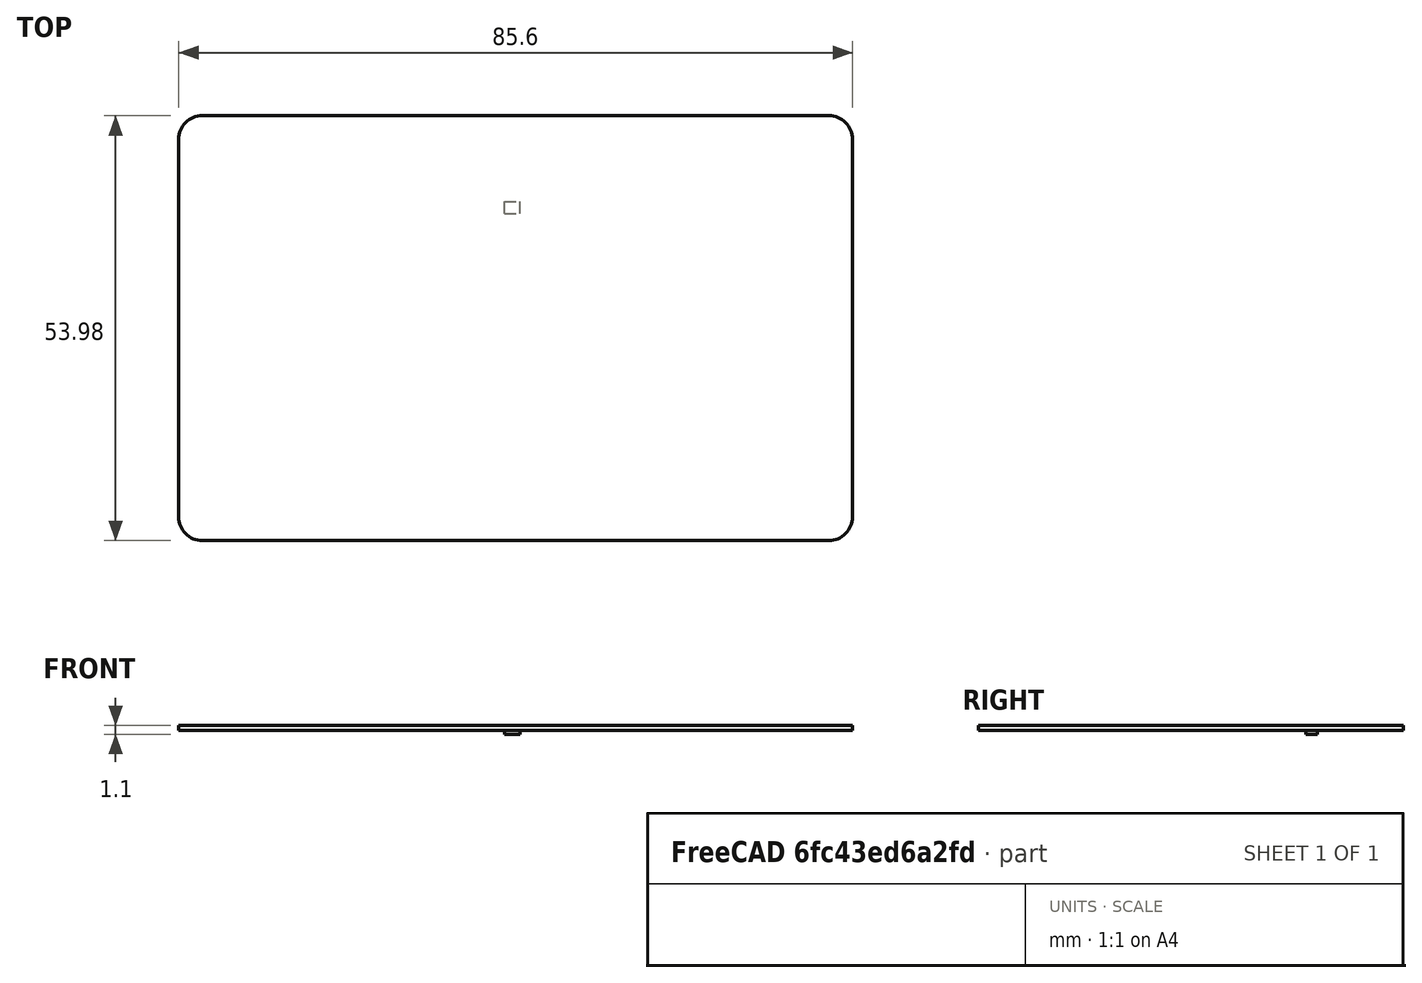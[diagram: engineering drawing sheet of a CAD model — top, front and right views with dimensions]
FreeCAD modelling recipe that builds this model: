
FCSTD DOCUMENT  (FreeCAD 0.16R6712 (Git))
Label: businessCard
License: All rights reserved
LicenseURL: http://en.wikipedia.org/wiki/All_rights_reserved
objects: Image::ImagePlane×2, Sketcher::SketchObject×1, PartDesign::Pad×1, Part::Box×1
note: 4 computed .brp shape members not serialized (recipe doc carries the construction recipe); baked Part::Feature solids carry a one-line shape summary decoded from their .brp

FEATURE [Sketcher::SketchObject] Sketch  label="Outline"
  sketch-geometry (8):
    g0: LineSegment StartX=2.93603 StartY=53.1716 StartZ=0 EndX=82.536 EndY=53.1716 EndZ=0
    g1: LineSegment StartX=85.536 StartY=50.1716 StartZ=0 EndX=85.536 EndY=2.19159 EndZ=0
    g2: LineSegment StartX=82.536 StartY=-0.808411 StartZ=0 EndX=2.93603 EndY=-0.808411 EndZ=0
    g3: LineSegment StartX=-0.063965 StartY=2.19159 StartZ=0 EndX=-0.063965 EndY=50.1716 EndZ=0
    g4: ArcOfCircle CenterX=2.93603 CenterY=50.1716 CenterZ=0 NormalX=0 NormalY=0 NormalZ=1 Radius=3 StartAngle=1.5708 EndAngle=3.14159
    g5: ArcOfCircle CenterX=82.536 CenterY=50.1716 CenterZ=0 NormalX=0 NormalY=0 NormalZ=1 Radius=3 StartAngle=0 EndAngle=1.5708
    g6: ArcOfCircle CenterX=82.536 CenterY=2.19159 CenterZ=0 NormalX=0 NormalY=0 NormalZ=1 Radius=3 StartAngle=4.71239 EndAngle=6.28319
    g7: ArcOfCircle CenterX=2.93603 CenterY=2.19159 CenterZ=0 NormalX=0 NormalY=0 NormalZ=1 Radius=3 StartAngle=3.14159 EndAngle=4.71239
  constraints (18):
    c: Horizontal(g0)
    c: Horizontal(g2)
    c: Vertical(g1)
    c: Vertical(g3)
    c: Tangent(g0,g4) = 1.5708
    c: Tangent(g3,g4) = 1.5708
    c: Tangent(g0,g5) = 1.5708
    c: Tangent(g1,g5) = 1.5708
    c: Tangent(g1,g6) = 1.5708
    c: Tangent(g2,g6) = 1.5708
    c: Radius(g4) = 3
    c: Equal(g5,g4)
    c: Equal(g6,g5)
    c: Tangent(g2,g7) = 1.5708
    c: Tangent(g3,g7) = 1.5708
    c: Equal(g7,g6)
    c: DistanceY(g2,g0) = 53.98
    c: DistanceX(g3,g1) = 85.6
FEATURE [PartDesign::Pad] Pad  label="Board"
  Length = 0.6
  Length2 = 100
  Sketch = -> Sketch
  Type = 0
FEATURE [Image::ImagePlane] ImagePlane  label="Front"
  Placement = pos=(42.72,26.2,0.61) rot=(0,0,1;0rad)
  XSize = 85.6
  YSize = 53.98
FEATURE [Image::ImagePlane] ImagePlane001  label="Back"
  Placement = pos=(42.72,26.2,0) rot=(0,1,0;3.14159rad)
  XSize = 85.6
  YSize = 53.98
FEATURE [Part::Box] Box  label="Cube"
  Height = 0.49
  Length = 2
  Placement = pos=(41.3,40.74,-0.5) rot=(0,0,1;0rad)
  Width = 1.5
